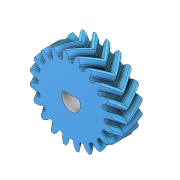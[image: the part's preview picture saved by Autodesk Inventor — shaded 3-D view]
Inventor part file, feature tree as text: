
AUTODESK INVENTOR PART (.ipt)
format: ipt  version: 2020.3 (Build 243373000, 373)  size: 1,539,072 bytes
history: native  units: mm
features: extrude x1, sketch x1, imported_body x1
ambient origin geometry x8: Origin, YZ Plane, XZ Plane, XY Plane, X Axis, Y Axis, Z Axis, Center Point
bodies: Solid1 (feature_tree)
feature tree (3):
  extrude  "Extrusion1"  [1 undecoded]
  sketch  "Sketch1"  dims[d0=86.0mm d1=0.0mm]
  imported_body  "Base1"
note: 1 required parameter value undecoded (feature->parameter linkage not recoverable at this tier; creation-order binding heuristic only, values carry confidence <= 0.55)
